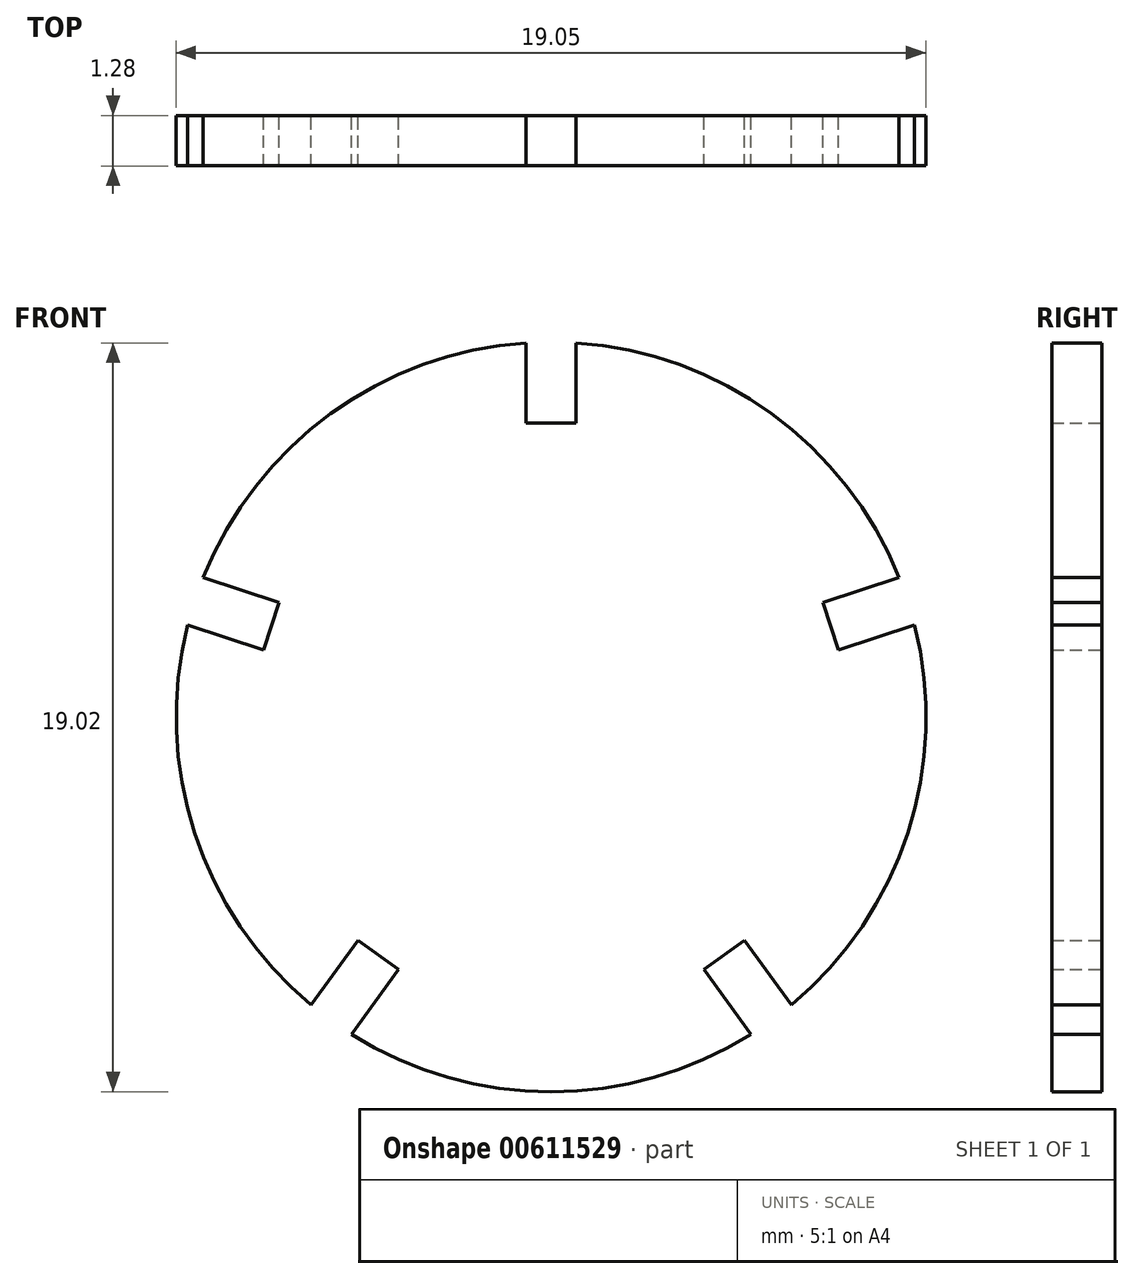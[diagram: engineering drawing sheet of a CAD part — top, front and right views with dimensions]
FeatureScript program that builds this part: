
annotation { "Feature Type Name" : "Feature", "Feature Type Description" : "" }
export const myFeature = defineFeature(function(context is Context, id is Id, definition is map)
    precondition{}
    {
        {
            var Q0;
            Q0=qCreatedBy(makeId("Front.planeOp"),FACE);
            var sketch = newSketch(context, id + "F0", { "sketchPlane" : qUnion([Q0])});
            skArc(sketch, "E0", {"start": v(-0.64, 9.5) * mm, "mid": v(-5.6, 7.7) * mm, "end": v(-8.84, 3.54) * mm});
            skLineSegment(sketch, "E1.top", {"start": v(-0.64, 7.47) * mm, "end": v(0.64, 7.47) * mm});
            skLineSegment(sketch, "E1.left", {"start": v(-0.64, 9.5) * mm, "end": v(-0.64, 7.47) * mm});
            skLineSegment(sketch, "E1.right", {"start": v(0.64, 9.5) * mm, "end": v(0.64, 7.47) * mm});
            skLineSegment(sketch, "E2.1.0", {"start": v(-8.84, 3.54) * mm, "end": v(-6.9, 2.91) * mm});
            skLineSegment(sketch, "E2.1.1", {"start": v(-7.3, 1.7) * mm, "end": v(-6.9, 2.91) * mm});
            skLineSegment(sketch, "E2.1.2", {"start": v(-9.23, 2.33) * mm, "end": v(-7.3, 1.7) * mm});
            skLineSegment(sketch, "E2.2.0", {"start": v(-6.1, -7.32) * mm, "end": v(-4.9, -5.67) * mm});
            skLineSegment(sketch, "E2.2.1", {"start": v(-3.88, -6.42) * mm, "end": v(-4.9, -5.67) * mm});
            skLineSegment(sketch, "E2.2.2", {"start": v(-5.07, -8.06) * mm, "end": v(-3.88, -6.42) * mm});
            skLineSegment(sketch, "E2.3.0", {"start": v(5.07, -8.06) * mm, "end": v(3.88, -6.42) * mm});
            skLineSegment(sketch, "E2.3.1", {"start": v(4.9, -5.67) * mm, "end": v(3.88, -6.42) * mm});
            skLineSegment(sketch, "E2.3.2", {"start": v(6.1, -7.32) * mm, "end": v(4.9, -5.67) * mm});
            skLineSegment(sketch, "E2.4.0", {"start": v(9.23, 2.33) * mm, "end": v(7.3, 1.7) * mm});
            skLineSegment(sketch, "E2.4.1", {"start": v(6.9, 2.91) * mm, "end": v(7.3, 1.7) * mm});
            skLineSegment(sketch, "E2.4.2", {"start": v(8.84, 3.54) * mm, "end": v(6.9, 2.91) * mm});
            skArc(sketch, "E3.trimOffspring", {"start": v(8.84, 3.54) * mm, "mid": v(5.6, 7.7) * mm, "end": v(0.63, 9.5) * mm});
            skArc(sketch, "E4.trimOffspring", {"start": v(6.1, -7.32) * mm, "mid": v(9.06, -2.94) * mm, "end": v(9.23, 2.33) * mm});
            skArc(sketch, "E5.trimOffspring", {"start": v(-5.07, -8.06) * mm, "mid": v(0, -9.53) * mm, "end": v(5.07, -8.06) * mm});
            skArc(sketch, "E6.trimOffspring", {"start": v(-9.23, 2.33) * mm, "mid": v(-9.06, -2.94) * mm, "end": v(-6.1, -7.32) * mm});
            skSolve(sketch);
        }
        {
            var Q0;
            Q0=makeQuery(id+"F0.imprint","IMPRINT",FACE,{"disambiguationData":[TD([[makeQuery(id+"F0.imprint","IMPRINT",EDGE,{"derivedFrom":sQuery(id+"F0.wireOp",EDGE,"E0")}),1.0]])]});
            extrude(context, id + "F1", {"entities" : qUnion([Q0]), "endBound" : BoundingType.SYMMETRIC, "depth" : 1.27 * mm, "offsetDistance" : 25.4 * mm});
        }
    });
